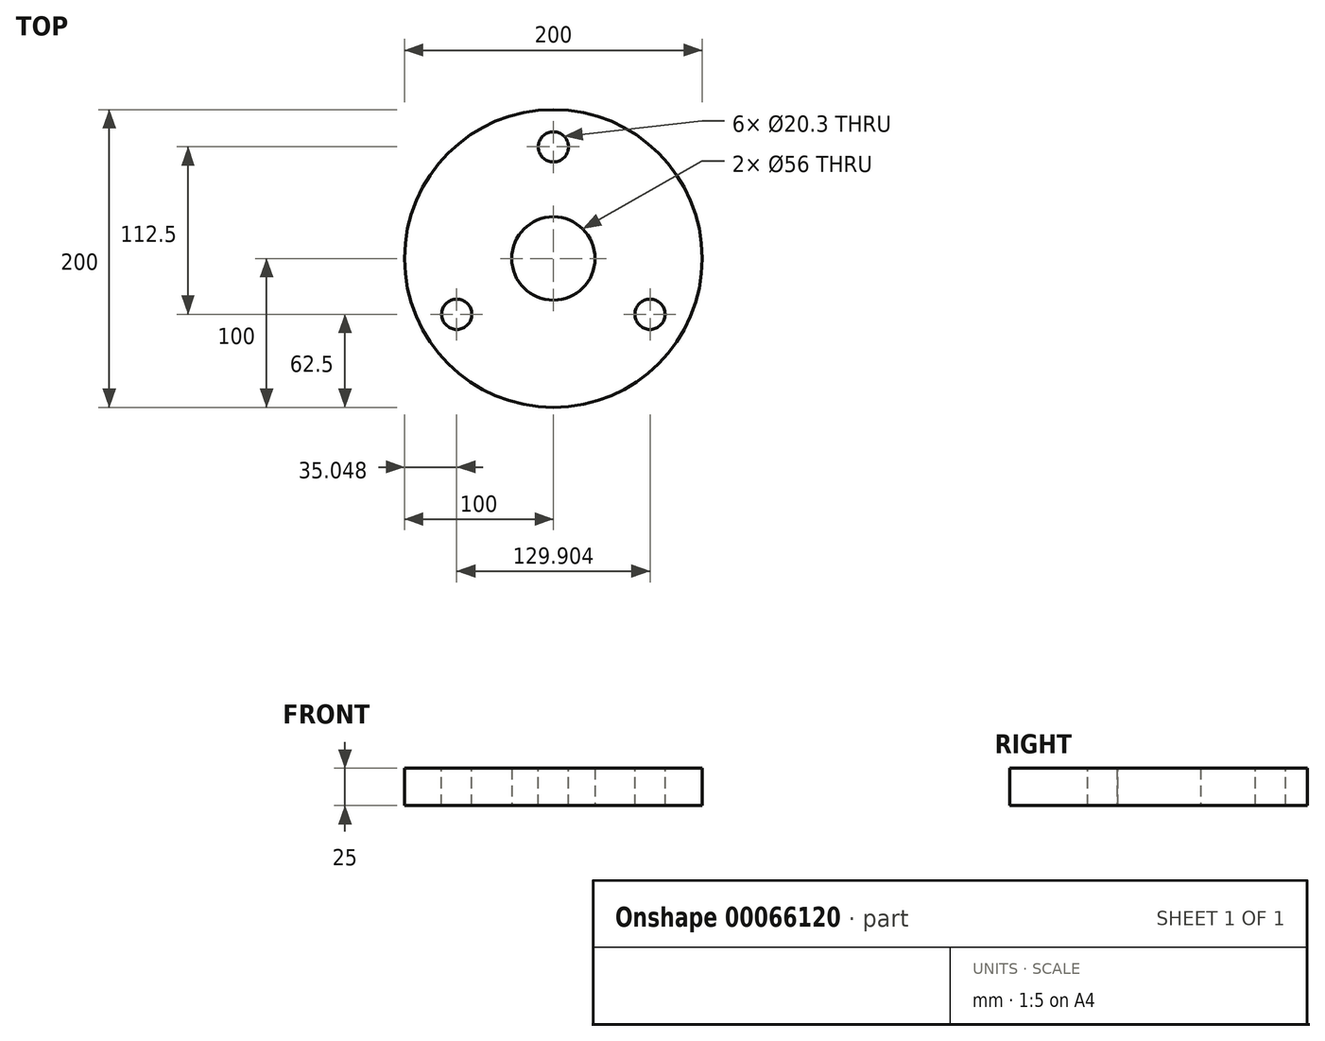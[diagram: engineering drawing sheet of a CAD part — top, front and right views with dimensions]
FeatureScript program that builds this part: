
annotation { "Feature Type Name" : "Feature", "Feature Type Description" : "" }
export const myFeature = defineFeature(function(context is Context, id is Id, definition is map)
    precondition{}
    {
        {
            var Q0;
            Q0=qCreatedBy(makeId("Top.planeOp"),FACE);
            var sketch = newSketch(context, id + "F0", { "sketchPlane" : qUnion([Q0])});
            skCircle(sketch, "E0", {"center": v(0, 0) * mm, "radius": 100 * mm});
            skCircle(sketch, "E1", {"center": v(0, 0) * mm, "radius": 28 * mm});
            skSolve(sketch);
        }
        {
            var Q0;
            Q0=makeQuery(id+"F0.imprint","IMPRINT",FACE,{"disambiguationData":[TD([[makeQuery(id+"F0.imprint","IMPRINT",EDGE,{"derivedFrom":sQuery(id+"F0.wireOp",EDGE,"E0")}),1.0]])]});
            extrude(context, id + "F1", {"entities" : qUnion([Q0]), "depth" : 25 * mm});
        }
        {
            var Q0;
            Q0=makeQuery(id+"F1.opExtrude","CAP_FACE",FACE,{"disambiguationData":[OSD([sQuery(id+"F0.wireOp",EDGE,"E0"),sQuery(id+"F0.wireOp",EDGE,"E1")])],"isStart":false});
            var sketch = newSketch(context, id + "F2", { "sketchPlane" : qUnion([Q0])});
            skCircle(sketch, "E2", {"center": v(0, 0) * mm, "radius": 75 * mm, "construction": true});
            skPoint(sketch, "E3", {"position": v(0, 75) * mm});
            skPoint(sketch, "E4.1.0", {"position": v(64.95, -37.5) * mm});
            skPoint(sketch, "E4.2.0", {"position": v(-64.95, -37.5) * mm});
            skLineSegment(sketch, "E4.anchor1", {"start": v(0, 0) * mm, "end": v(0, 75) * mm, "construction": true});
            skLineSegment(sketch, "E4.anchor2", {"start": v(0, 0) * mm, "end": v(-64.95, -37.5) * mm, "construction": true});
            skSolve(sketch);
        }
        {
            var Q0;
            Q0=sQuery(id+"F2.wireOp",VERTEX,"E3");
            var Q1;
            Q1=sQuery(id+"F2.wireOp",VERTEX,"E4.2.0");
            var Q2;
            Q2=sQuery(id+"F2.wireOp",VERTEX,"E4.1.0");
            var Q3;
            Q3=makeQuery(id+"F1.opExtrude","SWEPT_BODY",BODY,{"disambiguationData":[OSD([sQuery(id+"F0.wireOp",EDGE,"E0"),sQuery(id+"F0.wireOp",EDGE,"E1")])]});
            hole(context, id + "F3", {"style" : HoleStyle.SIMPLE, "holeDiameter" : 20.3 * mm, "endStyle" : HoleEndStyle.THROUGH, "locations" : qUnion([Q0, Q1, Q2]), "scope" : qUnion([Q3])});
        }
    });
